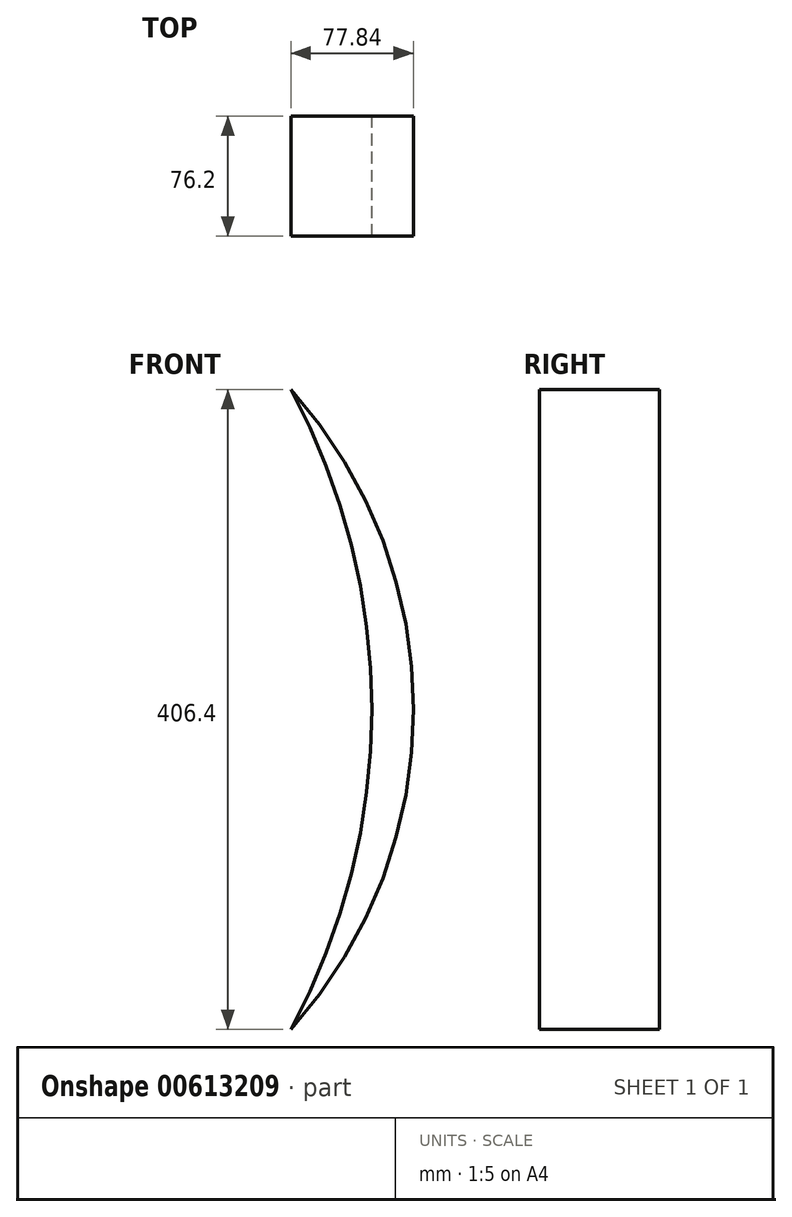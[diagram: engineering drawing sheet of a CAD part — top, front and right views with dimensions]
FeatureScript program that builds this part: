
annotation { "Feature Type Name" : "Feature", "Feature Type Description" : "" }
export const myFeature = defineFeature(function(context is Context, id is Id, definition is map)
    precondition{}
    {
        {
            var Q0;
            Q0=qCreatedBy(makeId("Front.planeOp"),FACE);
            var sketch = newSketch(context, id + "F0", { "sketchPlane" : qUnion([Q0])});
            skArc(sketch, "E0", {"start": v(-49.3, -289.1) * mm, "mid": v(28.55, -85.9) * mm, "end": v(-49.3, 117.3) * mm});
            skArc(sketch, "E1", {"start": v(-49.3, -289.1) * mm, "mid": v(2.1, -85.9) * mm, "end": v(-49.3, 117.3) * mm});
            skSolve(sketch);
        }
        {
            var Q0;
            Q0 = qSketchRegion(id + "F0", true);
            extrude(context, id + "F1", {"entities" : qUnion([Q0]), "depth" : 76.2 * mm, "offsetDistance" : 25.4 * mm});
        }
    });
